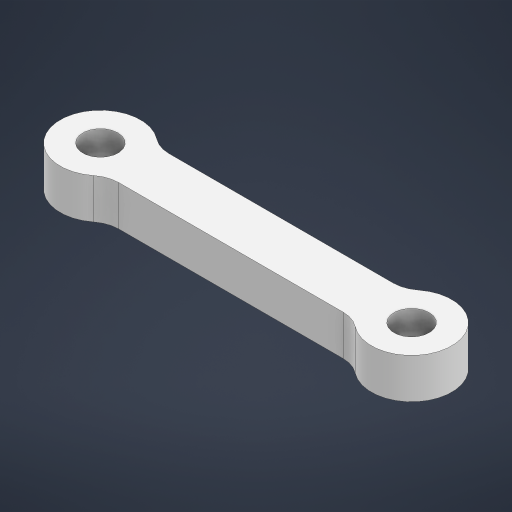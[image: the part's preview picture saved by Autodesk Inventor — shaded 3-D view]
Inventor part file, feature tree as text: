
AUTODESK INVENTOR PART (.ipt)
format: ipt  version: 2023 (Build 270158000, 158)  size: 216,064 bytes
history: native  units: mm
features: fillet x4
ambient origin geometry x8: Origin, YZ Plane, XZ Plane, XY Plane, X Axis, Y Axis, Z Axis, Center Point
bodies: Solid1 (feature_tree), Solid2 (feature_tree), Solid3 (feature_tree), Solid4 (feature_tree)
feature tree (4):
  fillet  "Fillet1"  [1 undecoded]
  fillet  "Fillet1:1"  [1 undecoded]
  fillet  "Fillet1:2"  [1 undecoded]
  fillet  "Fillet1:3"  [1 undecoded]
note: 4 required parameter values undecoded (feature->parameter linkage not recoverable at this tier; creation-order binding heuristic only, values carry confidence <= 0.55)
